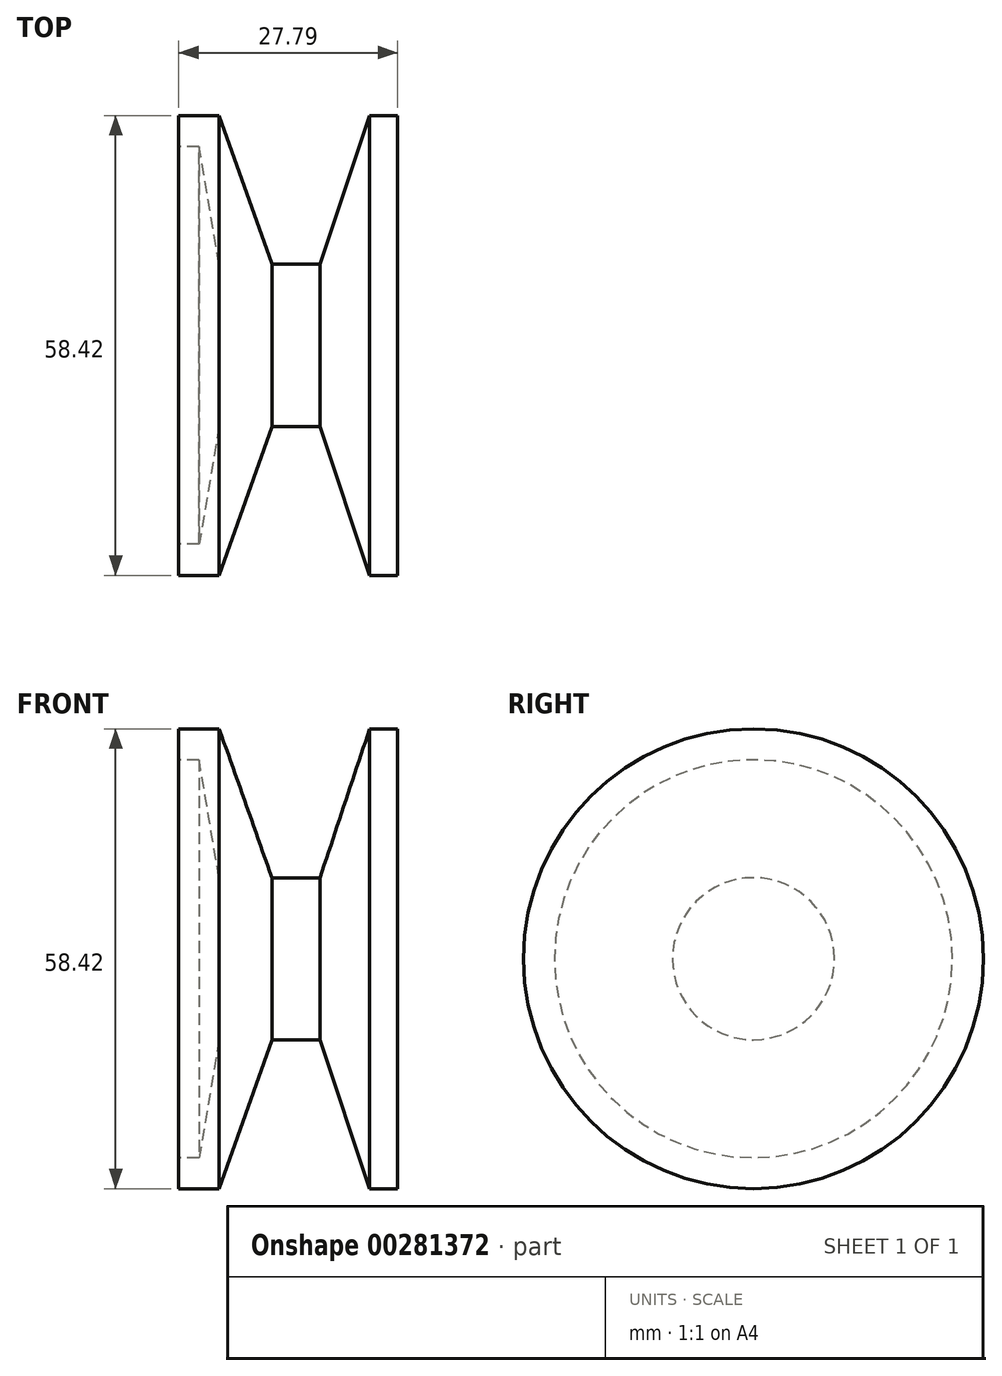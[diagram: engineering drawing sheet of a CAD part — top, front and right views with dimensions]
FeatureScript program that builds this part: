
annotation { "Feature Type Name" : "Feature", "Feature Type Description" : "" }
export const myFeature = defineFeature(function(context is Context, id is Id, definition is map)
    precondition{}
    {
        {
            var Q0;
            Q0=qCreatedBy(makeId("Front.planeOp"),FACE);
            var sketch = newSketch(context, id + "F0", { "sketchPlane" : qUnion([Q0])});
            skLineSegment(sketch, "E0", {"start": v(0, 0) * mm, "end": v(-3.14, 0) * mm});
            skLineSegment(sketch, "E1", {"start": v(0, 0) * mm, "end": v(2.95, 0) * mm});
            skLineSegment(sketch, "E2", {"start": v(-3.14, 0) * mm, "end": v(-9.85, 18.92) * mm});
            skLineSegment(sketch, "E3", {"start": v(2.95, 0) * mm, "end": v(9.27, 18.92) * mm});
            skLineSegment(sketch, "E4", {"start": v(9.27, 18.92) * mm, "end": v(12.8, 18.92) * mm});
            skLineSegment(sketch, "E5", {"start": v(12.8, 18.92) * mm, "end": v(12.8, -10.3) * mm});
            skLineSegment(sketch, "E6", {"start": v(-9.85, 18.92) * mm, "end": v(-14.98, 18.92) * mm});
            skLineSegment(sketch, "E7", {"start": v(-14.98, 18.92) * mm, "end": v(-14.98, 14.98) * mm});
            skLineSegment(sketch, "E8", {"start": v(-14.98, 14.98) * mm, "end": v(-12.42, 14.98) * mm});
            skLineSegment(sketch, "E9", {"start": v(-12.42, 14.98) * mm, "end": v(-9.85, 0) * mm});
            skLineSegment(sketch, "E10", {"start": v(-9.85, 0) * mm, "end": v(-9.85, -10.3) * mm});
            skLineSegment(sketch, "E11", {"start": v(-9.85, -10.3) * mm, "end": v(12.8, -10.3) * mm});
            skSolve(sketch);
        }
        {
            var Q0;
            Q0 = qSketchRegion(id + "F0", true);
            var Q1;
            Q1=sQuery(id+"F0.wireOp",EDGE,"E11");
            revolve(context, id + "F1", {"entities" : qUnion([Q0]), "axis" : qUnion([Q1]), "revolveType" : RevolveType.FULL});
        }
    });
